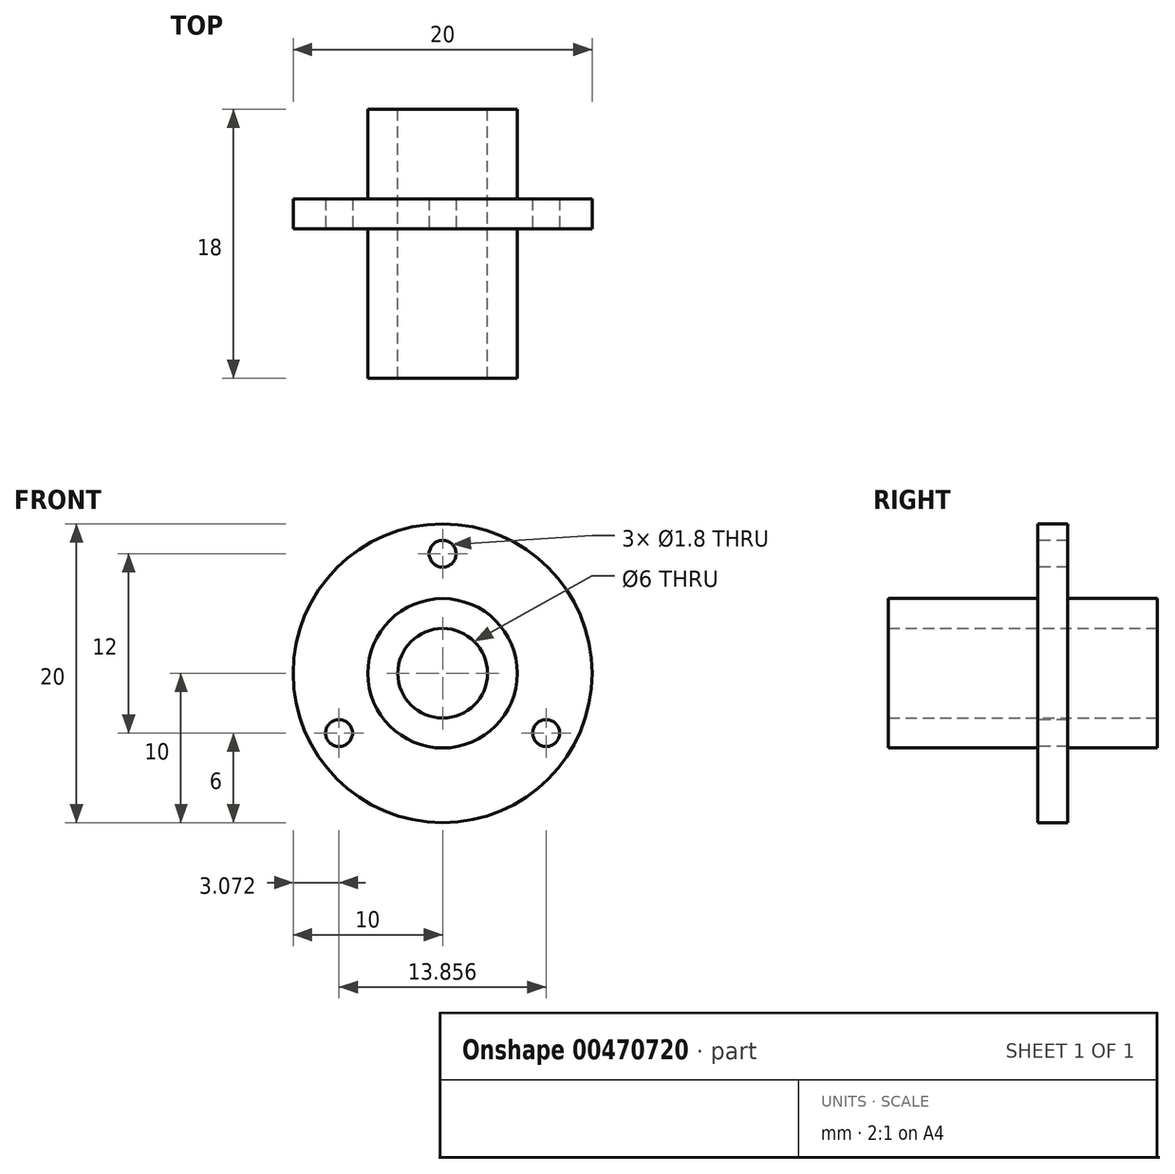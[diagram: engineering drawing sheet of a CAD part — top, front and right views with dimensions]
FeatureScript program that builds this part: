
annotation { "Feature Type Name" : "Feature", "Feature Type Description" : "" }
export const myFeature = defineFeature(function(context is Context, id is Id, definition is map)
    precondition{}
    {
        {
            var Q0;
            Q0=qCreatedBy(makeId("Front.planeOp"),FACE);
            var sketch = newSketch(context, id + "F0", { "sketchPlane" : qUnion([Q0])});
            skCircle(sketch, "E0", {"center": v(0, 0) * mm, "radius": 10 * mm});
            skCircle(sketch, "E1", {"center": v(0, 0) * mm, "radius": 5 * mm});
            skCircle(sketch, "E2", {"center": v(0, 0) * mm, "radius": 3 * mm});
            skLineSegment(sketch, "E3", {"start": v(0, 0) * mm, "end": v(0, 8) * mm, "construction": true});
            skPoint(sketch, "E4", {"position": v(0, 8) * mm});
            skPoint(sketch, "E5.1.0", {"position": v(-6.93, -4) * mm});
            skPoint(sketch, "E5.2.0", {"position": v(6.93, -4) * mm});
            skSolve(sketch);
        }
        {
            var Q0;
            Q0=makeQuery(id+"F0.imprint","IMPRINT",FACE,{"disambiguationData":[TD([[makeQuery(id+"F0.imprint","IMPRINT",EDGE,{"derivedFrom":sQuery(id+"F0.wireOp",EDGE,"E0")}),1.0]])]});
            extrude(context, id + "F1", {"entities" : qUnion([Q0]), "oppositeDirection" : true, "depth" : 2 * mm});
        }
        {
            var Q0;
            Q0=makeQuery(id+"F0.imprint","IMPRINT",FACE,{"disambiguationData":[TD([[makeQuery(id+"F0.imprint","IMPRINT",EDGE,{"derivedFrom":sQuery(id+"F0.wireOp",EDGE,"E1")}),1.0]])]});
            extrude(context, id + "F2", {"entities" : qUnion([Q0]), "operationType" : NewBodyOperationType.ADD, "depth" : 10 * mm, "hasSecondDirection" : true, "secondDirectionOppositeDirection" : true, "secondDirectionDepth" : 8 * mm});
        }
        {
            var Q0;
            Q0=sQuery(id+"F0.wireOp",VERTEX,"E4");
            var Q1;
            Q1=sQuery(id+"F0.wireOp",VERTEX,"E5.2.0");
            var Q2;
            Q2=sQuery(id+"F0.wireOp",VERTEX,"E5.1.0");
            var Q3;
            Q3=makeQuery(id+"F1.opExtrude","SWEPT_BODY",BODY,{"disambiguationData":[OSD([sQuery(id+"F0.wireOp",EDGE,"E0"),sQuery(id+"F0.wireOp",EDGE,"E1")])]});
            hole(context, id + "F3", {"style" : HoleStyle.SIMPLE, "endStyle" : HoleEndStyle.THROUGH, "holeDiameter" : 1.8 * mm, "isTappedThrough" : true, "tappedDepth" : 12 * mm, "tapClearance" : 3, "startFromSketch" : true, "locations" : qUnion([Q0, Q1, Q2]), "scope" : qUnion([Q3])});
        }
    });
